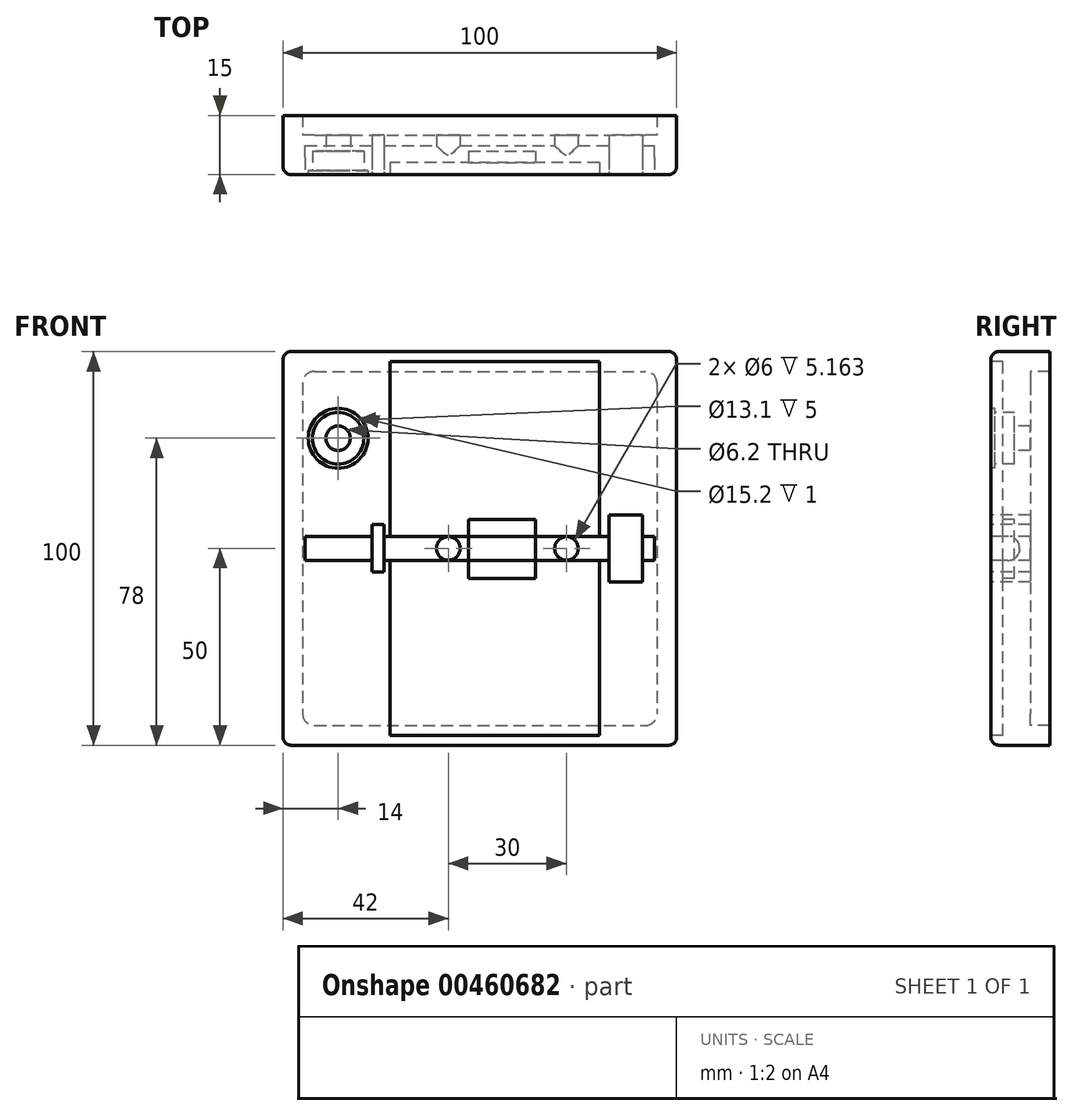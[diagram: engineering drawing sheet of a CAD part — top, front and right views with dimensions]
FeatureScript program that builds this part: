
annotation { "Feature Type Name" : "Feature", "Feature Type Description" : "" }
export const myFeature = defineFeature(function(context is Context, id is Id, definition is map)
    precondition{}
    {
        {
            var Q0;
            Q0=qCreatedBy(makeId("Front.planeOp"),FACE);
            var sketch = newSketch(context, id + "F0", { "sketchPlane" : qUnion([Q0])});
            skLineSegment(sketch, "E0.bottom", {"start": v(50, 50) * mm, "end": v(-50, 50) * mm});
            skLineSegment(sketch, "E0.top", {"start": v(50, -50) * mm, "end": v(-50, -50) * mm});
            skLineSegment(sketch, "E0.left", {"start": v(50, 50) * mm, "end": v(50, -50) * mm});
            skLineSegment(sketch, "E0.right", {"start": v(-50, 50) * mm, "end": v(-50, -50) * mm});
            skPoint(sketch, "E0.middle", {"position": v(0, 0) * mm});
            skSolve(sketch);
        }
        {
            var Q0;
            Q0=makeQuery(id+"F0.imprint","IMPRINT",FACE,{"disambiguationData":[TD([[makeQuery(id+"F0.imprint","IMPRINT",EDGE,{"derivedFrom":sQuery(id+"F0.wireOp",EDGE,"E0.bottom")}),1.0]])]});
            extrude(context, id + "F1", {"entities" : qUnion([Q0]), "oppositeDirection" : true, "depth" : 15 * mm, "offsetDistance" : 25 * mm});
        }
        {
            var Q0;
            Q0=makeQuery(id+"F1.opExtrude","SWEPT_EDGE",EDGE,{"disambiguationData":[OSD([sQuery(id+"F0.wireOp",EDGE,"E0.bottom"),sQuery(id+"F0.wireOp",EDGE,"E0.right")])]});
            var Q1;
            Q1=makeQuery(id+"F1.opExtrude","SWEPT_EDGE",EDGE,{"disambiguationData":[OSD([sQuery(id+"F0.wireOp",EDGE,"E0.bottom"),sQuery(id+"F0.wireOp",EDGE,"E0.left")])]});
            var Q2;
            Q2=makeQuery(id+"F1.opExtrude","CAP_EDGE",EDGE,{"disambiguationData":[OSD([sQuery(id+"F0.wireOp",EDGE,"E0.bottom")])],"isStart":true});
            var Q3;
            Q3=makeQuery(id+"F1.opExtrude","CAP_EDGE",EDGE,{"disambiguationData":[OSD([sQuery(id+"F0.wireOp",EDGE,"E0.left")])],"isStart":true});
            var Q4;
            Q4=makeQuery(id+"F1.opExtrude","SWEPT_EDGE",EDGE,{"disambiguationData":[OSD([sQuery(id+"F0.wireOp",EDGE,"E0.top"),sQuery(id+"F0.wireOp",EDGE,"E0.left")])]});
            var Q5;
            Q5=makeQuery(id+"F1.opExtrude","CAP_EDGE",EDGE,{"disambiguationData":[OSD([sQuery(id+"F0.wireOp",EDGE,"E0.top")])],"isStart":true});
            var Q6;
            Q6=makeQuery(id+"F1.opExtrude","CAP_EDGE",EDGE,{"disambiguationData":[OSD([sQuery(id+"F0.wireOp",EDGE,"E0.right")])],"isStart":true});
            var Q7;
            Q7=makeQuery(id+"F1.opExtrude","SWEPT_EDGE",EDGE,{"disambiguationData":[OSD([sQuery(id+"F0.wireOp",EDGE,"E0.top"),sQuery(id+"F0.wireOp",EDGE,"E0.right")])]});
            fillet(context, id + "F2", {"entities" : qUnion([Q0, Q1, Q2, Q3, Q4, Q5, Q6, Q7]), "tangentPropagation" : true, "radius" : 2 * mm, "defaultsChanged" : false, "vertexSettings" : [], "allowEdgeOverflow" : false});
        }
        {
            var Q0;
            Q0=qCreatedBy(makeId("Front.planeOp"),FACE);
            var sketch = newSketch(context, id + "F3", { "sketchPlane" : qUnion([Q0])});
            skLineSegment(sketch, "E1.bottom", {"start": v(-44.35, 3.05) * mm, "end": v(44.35, 3.05) * mm});
            skLineSegment(sketch, "E1.top", {"start": v(-44.35, -3.05) * mm, "end": v(44.35, -3.05) * mm});
            skLineSegment(sketch, "E1.left", {"start": v(-44.35, 3.05) * mm, "end": v(-44.35, -3.05) * mm});
            skLineSegment(sketch, "E1.right", {"start": v(44.35, 3.05) * mm, "end": v(44.35, -3.05) * mm});
            skPoint(sketch, "E1.middle", {"position": v(0, 0) * mm});
            skSolve(sketch);
        }
        {
            var Q0;
            Q0=makeQuery(id+"F3.imprint","IMPRINT",FACE,{"disambiguationData":[TD([[makeQuery(id+"F3.imprint","IMPRINT",EDGE,{"derivedFrom":sQuery(id+"F3.wireOp",EDGE,"E1.bottom")}),-1.0]])]});
            extrude(context, id + "F4", {"entities" : qUnion([Q0]), "operationType" : NewBodyOperationType.REMOVE, "oppositeDirection" : true, "depth" : 7.3 * mm, "offsetDistance" : 25 * mm});
        }
        {
            var Q0;
            Q0=makeQuery(id+"F4.boolean.opBoolean","COPY",EDGE,{"derivedFrom":makeQuery(id+"F4.opExtrude","CAP_EDGE",EDGE,{"disambiguationData":[OSD([sQuery(id+"F3.wireOp",EDGE,"E1.top")])],"isStart":false})});
            var Q1;
            Q1=makeQuery(id+"F4.boolean.opBoolean","COPY",EDGE,{"derivedFrom":makeQuery(id+"F4.opExtrude","CAP_EDGE",EDGE,{"disambiguationData":[OSD([sQuery(id+"F3.wireOp",EDGE,"E1.bottom")])],"isStart":false})});
            fillet(context, id + "F5", {"entities" : qUnion([Q0, Q1]), "tangentPropagation" : true, "radius" : 3 * mm, "defaultsChanged" : false, "vertexSettings" : [], "allowEdgeOverflow" : false});
        }
        {
            var Q0;
            Q0=qCreatedBy(makeId("Front.planeOp"),FACE);
            var sketch = newSketch(context, id + "F6", { "sketchPlane" : qUnion([Q0])});
            skCircle(sketch, "E2", {"center": v(-8, 0) * mm, "radius": 3 * mm});
            skCircle(sketch, "E3", {"center": v(22, 0) * mm, "radius": 3 * mm});
            skSolve(sketch);
        }
        {
            var Q0;
            Q0=makeQuery(id+"F6.imprint","IMPRINT",FACE,{"disambiguationData":[TD([[makeQuery(id+"F6.imprint","IMPRINT",EDGE,{"derivedFrom":sQuery(id+"F6.wireOp",EDGE,"E2")}),1.0]])]});
            var Q1;
            Q1=makeQuery(id+"F6.imprint","IMPRINT",FACE,{"disambiguationData":[TD([[makeQuery(id+"F6.imprint","IMPRINT",EDGE,{"derivedFrom":sQuery(id+"F6.wireOp",EDGE,"E3")}),1.0]])]});
            extrude(context, id + "F7", {"entities" : qUnion([Q0, Q1]), "operationType" : NewBodyOperationType.REMOVE, "oppositeDirection" : true, "depth" : 16 * mm, "offsetDistance" : 25 * mm});
        }
        {
            var Q0;
            Q0=qCreatedBy(makeId("Front.planeOp"),FACE);
            var sketch = newSketch(context, id + "F8", { "sketchPlane" : qUnion([Q0])});
            skLineSegment(sketch, "E4.bottom", {"start": v(-22.85, -47.55) * mm, "end": v(30.35, -47.55) * mm});
            skLineSegment(sketch, "E4.top", {"start": v(-22.85, 47.45) * mm, "end": v(30.35, 47.45) * mm});
            skLineSegment(sketch, "E4.left", {"start": v(-22.85, -47.55) * mm, "end": v(-22.85, 47.45) * mm});
            skLineSegment(sketch, "E4.right", {"start": v(30.35, -47.55) * mm, "end": v(30.35, 47.45) * mm});
            skSolve(sketch);
        }
        {
            var Q0;
            Q0=makeQuery(id+"F8.imprint","IMPRINT",FACE,{"disambiguationData":[TD([[makeQuery(id+"F8.imprint","IMPRINT",EDGE,{"derivedFrom":sQuery(id+"F8.wireOp",EDGE,"E4.bottom")}),1.0]])]});
            extrude(context, id + "F9", {"entities" : qUnion([Q0]), "operationType" : NewBodyOperationType.REMOVE, "oppositeDirection" : true, "depth" : 3 * mm, "offsetDistance" : 25 * mm});
        }
        {
            var Q0;
            Q0=qCreatedBy(makeId("Front.planeOp"),FACE);
            var sketch = newSketch(context, id + "F10", { "sketchPlane" : qUnion([Q0])});
            skLineSegment(sketch, "E5.bottom", {"start": v(-2.85, -7.63) * mm, "end": v(14.15, -7.63) * mm});
            skLineSegment(sketch, "E5.top", {"start": v(-2.85, 7.37) * mm, "end": v(14.15, 7.37) * mm});
            skLineSegment(sketch, "E5.left", {"start": v(-2.85, -7.63) * mm, "end": v(-2.85, 7.37) * mm});
            skLineSegment(sketch, "E5.right", {"start": v(14.15, -7.63) * mm, "end": v(14.15, 7.37) * mm});
            skSolve(sketch);
        }
        {
            var Q0;
            Q0=makeQuery(id+"F10.imprint","IMPRINT",FACE,{"disambiguationData":[TD([[makeQuery(id+"F10.imprint","IMPRINT",EDGE,{"derivedFrom":sQuery(id+"F10.wireOp",EDGE,"E5.bottom")}),1.0]])]});
            extrude(context, id + "F11", {"entities" : qUnion([Q0]), "oppositeDirection" : true, "depth" : 6 * mm, "offsetDistance" : 25 * mm, "hasSecondDirection" : true, "secondDirectionOppositeDirection" : true, "secondDirectionDepth" : 3 * mm});
        }
        {
            var Q0;
            Q0=qCreatedBy(makeId("Front.planeOp"),FACE);
            var sketch = newSketch(context, id + "F12", { "sketchPlane" : qUnion([Q0])});
            skLineSegment(sketch, "E6.bottom", {"start": v(32.85, -8.5) * mm, "end": v(41.35, -8.5) * mm});
            skLineSegment(sketch, "E6.top", {"start": v(32.85, 8.5) * mm, "end": v(41.35, 8.5) * mm});
            skLineSegment(sketch, "E6.left", {"start": v(32.85, -8.5) * mm, "end": v(32.85, 8.5) * mm});
            skLineSegment(sketch, "E6.right", {"start": v(41.35, -8.5) * mm, "end": v(41.35, 8.5) * mm});
            skSolve(sketch);
        }
        {
            var Q0;
            Q0=makeQuery(id+"F12.imprint","IMPRINT",FACE,{"disambiguationData":[TD([[makeQuery(id+"F12.imprint","IMPRINT",EDGE,{"derivedFrom":sQuery(id+"F12.wireOp",EDGE,"E6.bottom")}),1.0]])]});
            extrude(context, id + "F13", {"entities" : qUnion([Q0]), "operationType" : NewBodyOperationType.REMOVE, "oppositeDirection" : true, "depth" : 16 * mm, "offsetDistance" : 25 * mm});
        }
        {
            var Q0;
            Q0=qCreatedBy(makeId("Front.planeOp"),FACE);
            var sketch = newSketch(context, id + "F14", { "sketchPlane" : qUnion([Q0])});
            skLineSegment(sketch, "E7.bottom", {"start": v(-27.35, -5.95) * mm, "end": v(-24.35, -5.95) * mm});
            skLineSegment(sketch, "E7.top", {"start": v(-27.35, 6.05) * mm, "end": v(-24.35, 6.05) * mm});
            skLineSegment(sketch, "E7.left", {"start": v(-27.35, -5.95) * mm, "end": v(-27.35, 6.05) * mm});
            skLineSegment(sketch, "E7.right", {"start": v(-24.35, -5.95) * mm, "end": v(-24.35, 6.05) * mm});
            skSolve(sketch);
        }
        {
            var Q0;
            Q0=makeQuery(id+"F14.imprint","IMPRINT",FACE,{"disambiguationData":[TD([[makeQuery(id+"F14.imprint","IMPRINT",EDGE,{"derivedFrom":sQuery(id+"F14.wireOp",EDGE,"E7.bottom")}),1.0]])]});
            extrude(context, id + "F15", {"entities" : qUnion([Q0]), "operationType" : NewBodyOperationType.REMOVE, "oppositeDirection" : true, "depth" : 16 * mm, "offsetDistance" : 25 * mm});
        }
        {
            var Q0;
            Q0=qCreatedBy(makeId("Front.planeOp"),FACE);
            var sketch = newSketch(context, id + "F16", { "sketchPlane" : qUnion([Q0])});
            skLineSegment(sketch, "E8", {"start": v(-36, 59.68) * mm, "end": v(-36, 9.32) * mm, "construction": true});
            skLineSegment(sketch, "E9", {"start": v(-60.12, 28) * mm, "end": v(-21.19, 28) * mm, "construction": true});
            skCircle(sketch, "E10", {"center": v(-36, 28) * mm, "radius": 3.1 * mm});
            skSolve(sketch);
        }
        {
            var Q0;
            Q0=makeQuery(id+"F16.imprint","IMPRINT",FACE,{"disambiguationData":[TD([[makeQuery(id+"F16.imprint","IMPRINT",EDGE,{"derivedFrom":sQuery(id+"F16.wireOp",EDGE,"E10")}),1.0]])]});
            extrude(context, id + "F17", {"entities" : qUnion([Q0]), "operationType" : NewBodyOperationType.REMOVE, "oppositeDirection" : true, "depth" : 16 * mm, "offsetDistance" : 25 * mm});
        }
        {
            var Q0;
            Q0=qCreatedBy(makeId("Front.planeOp"),FACE);
            var sketch = newSketch(context, id + "F18", { "sketchPlane" : qUnion([Q0])});
            skLineSegment(sketch, "E11", {"start": v(-36, 45.1) * mm, "end": v(-36, 11.4) * mm, "construction": true});
            skLineSegment(sketch, "E12", {"start": v(-59.64, 28) * mm, "end": v(-15.28, 28) * mm, "construction": true});
            skCircle(sketch, "E13", {"center": v(-36, 28) * mm, "radius": 6.55 * mm});
            skSolve(sketch);
        }
        {
            var Q0;
            Q0=makeQuery(id+"F18.imprint","IMPRINT",FACE,{"disambiguationData":[TD([[makeQuery(id+"F18.imprint","IMPRINT",EDGE,{"derivedFrom":sQuery(id+"F18.wireOp",EDGE,"E13")}),1.0]])]});
            extrude(context, id + "F19", {"entities" : qUnion([Q0]), "operationType" : NewBodyOperationType.REMOVE, "oppositeDirection" : true, "depth" : 6 * mm, "offsetDistance" : 25 * mm});
        }
        {
            var Q0;
            Q0=qCreatedBy(makeId("Front.planeOp"),FACE);
            var sketch = newSketch(context, id + "F20", { "sketchPlane" : qUnion([Q0])});
            skLineSegment(sketch, "E14", {"start": v(-36, 57.21) * mm, "end": v(-36, 14.41) * mm, "construction": true});
            skLineSegment(sketch, "E15", {"start": v(-58.76, 28) * mm, "end": v(-17.87, 28) * mm, "construction": true});
            skCircle(sketch, "E16", {"center": v(-36, 28) * mm, "radius": 7.6 * mm});
            skSolve(sketch);
        }
        {
            var Q0;
            Q0 = qSketchRegion(id + "F20", true);
            extrude(context, id + "F21", {"entities" : qUnion([Q0]), "operationType" : NewBodyOperationType.REMOVE, "oppositeDirection" : true, "depth" : 1 * mm, "offsetDistance" : 25 * mm});
        }
        {
            var Q0;
            Q0=qCreatedBy(makeId("Front.planeOp"),FACE);
            var sketch = newSketch(context, id + "F22", { "sketchPlane" : qUnion([Q0])});
            skLineSegment(sketch, "E17.bottom", {"start": v(-45, 45) * mm, "end": v(45, 45) * mm});
            skLineSegment(sketch, "E17.top", {"start": v(-45, -45) * mm, "end": v(45, -45) * mm});
            skLineSegment(sketch, "E17.left", {"start": v(-45, 45) * mm, "end": v(-45, -45) * mm});
            skLineSegment(sketch, "E17.right", {"start": v(45, 45) * mm, "end": v(45, -45) * mm});
            skPoint(sketch, "E17.middle", {"position": v(0, 0) * mm});
            skSolve(sketch);
        }
        {
            var Q0;
            Q0 = qSketchRegion(id + "F22", true);
            extrude(context, id + "F23", {"entities" : qUnion([Q0]), "operationType" : NewBodyOperationType.REMOVE, "oppositeDirection" : true, "depth" : 16 * mm, "offsetDistance" : 25 * mm, "hasSecondDirection" : true, "secondDirectionOppositeDirection" : true, "secondDirectionDepth" : 10 * mm});
        }
        {
            var Q0;
            Q0=makeQuery(id+"F23.boolean.opBoolean","COPY",EDGE,{"derivedFrom":makeQuery(id+"F23.opExtrude","SWEPT_EDGE",EDGE,{"disambiguationData":[OSD([sQuery(id+"F22.wireOp",EDGE,"E17.top"),sQuery(id+"F22.wireOp",EDGE,"E17.right")])]})});
            var Q1;
            Q1=makeQuery(id+"F23.boolean.opBoolean","COPY",EDGE,{"derivedFrom":makeQuery(id+"F23.opExtrude","SWEPT_EDGE",EDGE,{"disambiguationData":[OSD([sQuery(id+"F22.wireOp",EDGE,"E17.bottom"),sQuery(id+"F22.wireOp",EDGE,"E17.right")])]})});
            var Q2;
            Q2=makeQuery(id+"F23.boolean.opBoolean","COPY",EDGE,{"derivedFrom":makeQuery(id+"F23.opExtrude","SWEPT_EDGE",EDGE,{"disambiguationData":[OSD([sQuery(id+"F22.wireOp",EDGE,"E17.top"),sQuery(id+"F22.wireOp",EDGE,"E17.left")])]})});
            var Q3;
            Q3=makeQuery(id+"F23.boolean.opBoolean","COPY",EDGE,{"derivedFrom":makeQuery(id+"F23.opExtrude","SWEPT_EDGE",EDGE,{"disambiguationData":[OSD([sQuery(id+"F22.wireOp",EDGE,"E17.bottom"),sQuery(id+"F22.wireOp",EDGE,"E17.left")])]})});
            fillet(context, id + "F24", {"entities" : qUnion([Q0, Q1, Q2, Q3]), "tangentPropagation" : true, "radius" : 3 * mm, "defaultsChanged" : false, "vertexSettings" : [], "allowEdgeOverflow" : false});
        }
    });
